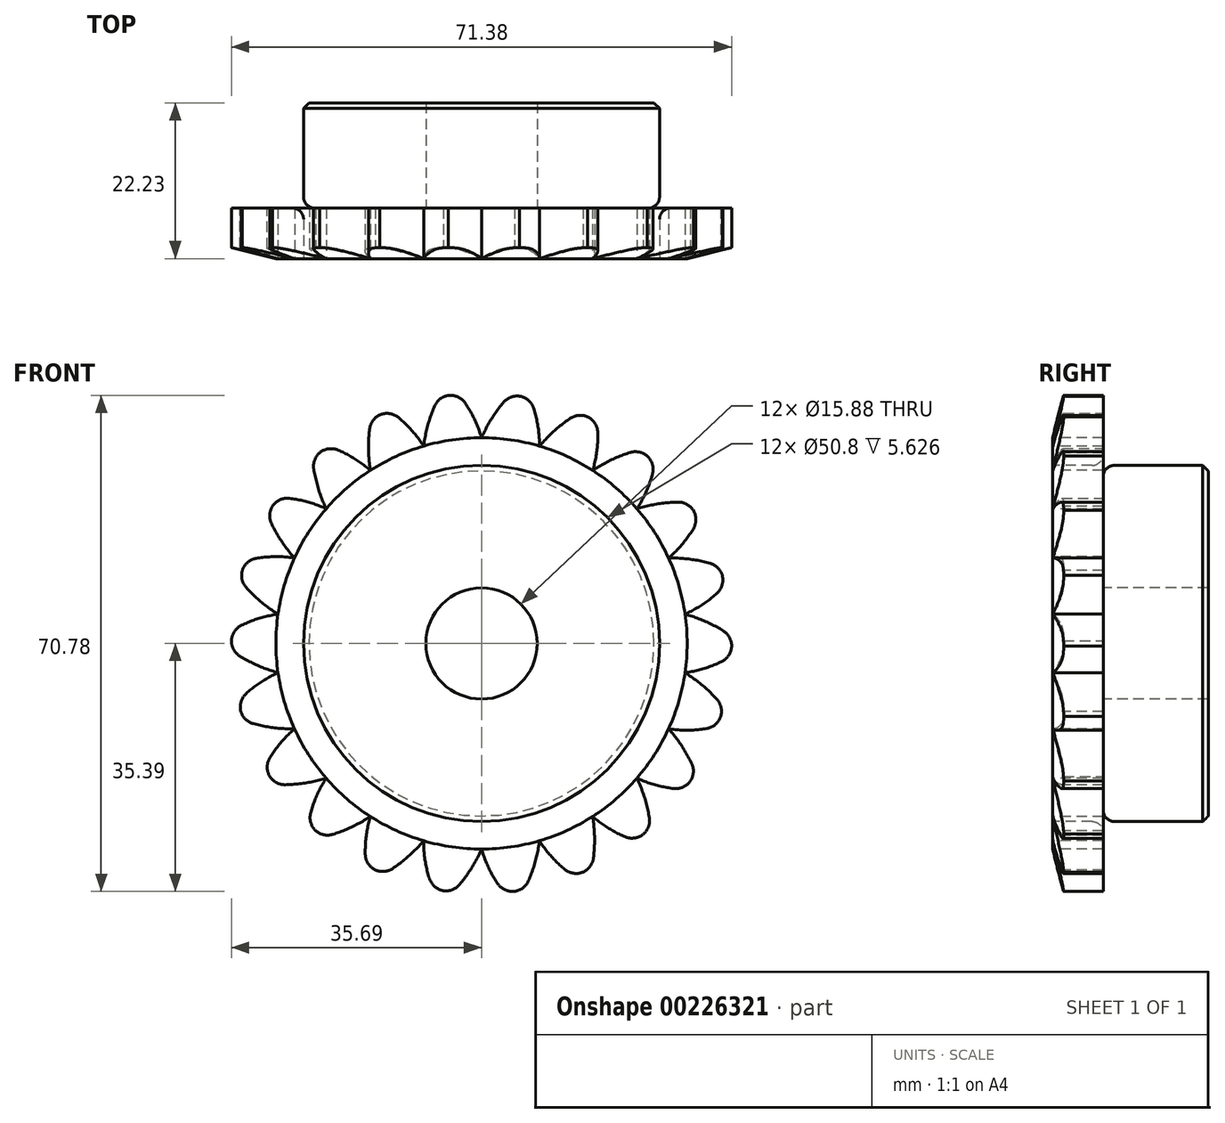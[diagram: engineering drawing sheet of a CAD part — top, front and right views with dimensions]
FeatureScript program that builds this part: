
annotation { "Feature Type Name" : "Feature", "Feature Type Description" : "" }
export const myFeature = defineFeature(function(context is Context, id is Id, definition is map)
    precondition{}
    {
        {
            var Q0;
            Q0=qCreatedBy(makeId("Right.planeOp"),FACE);
            var sketch = newSketch(context, id + "F0", { "sketchPlane" : qUnion([Q0])});
            skLineSegment(sketch, "E0", {"start": v(0, 0) * mm, "end": v(16.92, 0) * mm});
            skLineSegment(sketch, "E1.bottom", {"start": v(0, 7.94) * mm, "end": v(7.21, 7.94) * mm});
            skLineSegment(sketch, "E1.top", {"start": v(0, 35.69) * mm, "end": v(7.21, 35.69) * mm});
            skLineSegment(sketch, "E1.left", {"start": v(0, 7.94) * mm, "end": v(0, 35.69) * mm});
            skLineSegment(sketch, "E1.right", {"start": v(7.21, 7.94) * mm, "end": v(7.21, 35.69) * mm});
            skLineSegment(sketch, "E2.bottom", {"start": v(0, 7.94) * mm, "end": v(22.23, 7.94) * mm});
            skLineSegment(sketch, "E2.top", {"start": v(0, 25.4) * mm, "end": v(22.23, 25.4) * mm});
            skLineSegment(sketch, "E2.left", {"start": v(0, 7.94) * mm, "end": v(0, 25.4) * mm});
            skLineSegment(sketch, "E2.right", {"start": v(22.23, 7.94) * mm, "end": v(22.22, 25.4) * mm});
            skLineSegment(sketch, "E3.MirrorCS", {"start": v(0, -7.94) * mm, "end": v(7.21, -7.94) * mm});
            skLineSegment(sketch, "E4.MirrorCS", {"start": v(22.23, -7.94) * mm, "end": v(22.23, -25.4) * mm});
            skLineSegment(sketch, "E5.MirrorCS", {"start": v(0, -7.94) * mm, "end": v(0, -25.4) * mm});
            skLineSegment(sketch, "E6.MirrorCS", {"start": v(0, -35.69) * mm, "end": v(7.21, -35.69) * mm});
            skLineSegment(sketch, "E7.MirrorCS", {"start": v(0, -7.94) * mm, "end": v(0, -35.69) * mm});
            skLineSegment(sketch, "E8.MirrorCS", {"start": v(7.21, -7.94) * mm, "end": v(7.21, -35.69) * mm});
            skLineSegment(sketch, "E9.MirrorCS", {"start": v(0, -25.4) * mm, "end": v(22.23, -25.4) * mm});
            skLineSegment(sketch, "E10.MirrorCS", {"start": v(0, -7.94) * mm, "end": v(22.23, -7.94) * mm});
            skSolve(sketch);
        }
        {
            var Q0;
            {var subQ0=sQuery(id+"F0.wireOp",EDGE,"E1.top");Q0=makeQuery(id+"F0.imprint","IMPRINT",FACE,{"disambiguationData":[TD([[makeQuery(id+"F0.imprint","IMPRINT",EDGE,{"derivedFrom":subQ0}),-1.0]])]});}
            var Q1;
            {var subQ5=sQuery(id+"F0.wireOp",EDGE,"E2.left");Q1=makeQuery(id+"F0.imprint","IMPRINT",FACE,{"disambiguationData":[TD([[makeQuery(id+"F0.imprint","IMPRINT",EDGE,{"derivedFrom":subQ5}),-1.0]])]});}
            var Q2;
            {var subQ5=sQuery(id+"F0.wireOp",EDGE,"E2.right");Q2=makeQuery(id+"F0.imprint","IMPRINT",FACE,{"disambiguationData":[TD([[makeQuery(id+"F0.imprint","IMPRINT",EDGE,{"derivedFrom":subQ5}),1.0]])]});}
            var Q3;
            Q3=sQuery(id+"F0.wireOp",EDGE,"E0");
            revolve(context, id + "F1", {"entities" : qUnion([Q0, Q1, Q2]), "axis" : qUnion([Q3]), "revolveType" : RevolveType.FULL});
        }
        {
            var Q0;
            Q0=makeQuery(id+"F1.opRevolve","SWEPT_EDGE",EDGE,{"disambiguationData":[OSD([sQuery(id+"F0.wireOp",EDGE,"E1.right"),sQuery(id+"F0.wireOp",EDGE,"E2.top")])]});
            fillet(context, id + "F2", {"entities" : qUnion([Q0]), "radius" : 1.59 * mm, "tangentPropagation" : true, "allowEdgeOverflow" : false});
        }
        {
            var Q0;
            Q0=makeQuery(id+"F1.opRevolve","SWEPT_EDGE",EDGE,{"disambiguationData":[OSD([sQuery(id+"F0.wireOp",EDGE,"E2.top"),sQuery(id+"F0.wireOp",EDGE,"E2.right")])]});
            chamfer(context, id + "F3", {"entities" : qUnion([Q0]), "width" : 0.8 * mm, "tangentPropagation" : true});
        }
        {
            var Q0;
            Q0=makeQuery(id+"F1.opRevolve","SWEPT_EDGE",EDGE,{"disambiguationData":[OSD([sQuery(id+"F0.wireOp",EDGE,"E1.top"),sQuery(id+"F0.wireOp",EDGE,"E1.left")])]});
            chamfer(context, id + "F4", {"entities" : qUnion([Q0]), "chamferType" : ChamferType.TWO_OFFSETS, "width1" : 6.35 * mm, "oppositeDirection" : false, "width2" : 1.57 * mm, "tangentPropagation" : true});
        }
        {
            var Q0;
            Q0=qCreatedBy(makeId("Front.planeOp"),FACE);
            cPlane(context, id + "F5", {"entities" : qUnion([Q0]), "cplaneType" : CPlaneType.OFFSET, "offset" : 0 * mm, "oppositeDirection" : true, "width" : 152.4 * mm, "height" : 152.4 * mm});
        }
        {
            var Q0;
            Q0=qCreatedBy(id+"F5.planeOp",FACE);
            var sketch = newSketch(context, id + "F6", { "sketchPlane" : qUnion([Q0])});
            skArc(sketch, "E11", {"start": v(0, 29.34) * mm, "mid": v(-1.65, 33.21) * mm, "end": v(-4.18, 36.58) * mm});
            skArc(sketch, "E12", {"start": v(4.94, 36.31) * mm, "mid": v(2.12, 33.08) * mm, "end": v(0, 29.34) * mm});
            skArc(sketch, "E13", {"start": v(4.94, 36.31) * mm, "mid": v(0.4, 36.73) * mm, "end": v(-4.18, 36.58) * mm});
            skArc(sketch, "E14.1.0", {"start": v(-8.26, 28.15) * mm, "mid": v(-10.94, 31.4) * mm, "end": v(-14.32, 33.92) * mm});
            skArc(sketch, "E14.1.1", {"start": v(-5.49, 36.24) * mm, "mid": v(-7.29, 32.33) * mm, "end": v(-8.26, 28.15) * mm});
            skArc(sketch, "E14.1.2", {"start": v(-5.49, 36.24) * mm, "mid": v(-9.97, 35.35) * mm, "end": v(-14.32, 33.92) * mm});
            skArc(sketch, "E14.2.0", {"start": v(-15.86, 24.68) * mm, "mid": v(-19.34, 27.05) * mm, "end": v(-23.3, 28.52) * mm});
            skArc(sketch, "E14.2.1", {"start": v(-15.47, 33.22) * mm, "mid": v(-16.1, 28.97) * mm, "end": v(-15.86, 24.68) * mm});
            skArc(sketch, "E14.2.2", {"start": v(-15.47, 33.22) * mm, "mid": v(-19.53, 31.1) * mm, "end": v(-23.3, 28.52) * mm});
            skPoint(sketch, "E14.center", {"position": v(0, 0) * mm});
            skArc(sketch, "E15.1.3.0", {"start": v(-22.17, 19.21) * mm, "mid": v(-26.18, 20.5) * mm, "end": v(-30.38, 20.8) * mm});
            skArc(sketch, "E15.4.3.0", {"start": v(-24.2, 27.52) * mm, "mid": v(-23.61, 23.26) * mm, "end": v(-22.17, 19.21) * mm});
            skArc(sketch, "E15.8.3.0", {"start": v(-24.2, 27.52) * mm, "mid": v(-27.5, 24.34) * mm, "end": v(-30.38, 20.8) * mm});
            skArc(sketch, "E15.1.4.0", {"start": v(-26.68, 12.19) * mm, "mid": v(-30.9, 12.3) * mm, "end": v(-35.01, 11.4) * mm});
            skArc(sketch, "E15.4.4.0", {"start": v(-30.98, 19.58) * mm, "mid": v(-29.2, 15.66) * mm, "end": v(-26.68, 12.19) * mm});
            skArc(sketch, "E15.8.4.0", {"start": v(-30.98, 19.58) * mm, "mid": v(-33.24, 15.61) * mm, "end": v(-35.01, 11.4) * mm});
            skArc(sketch, "E15.1.5.0", {"start": v(-29.04, 4.17) * mm, "mid": v(-33.11, 3.1) * mm, "end": v(-36.8, 1.07) * mm});
            skArc(sketch, "E15.4.5.0", {"start": v(-35.24, 10.06) * mm, "mid": v(-32.44, 6.8) * mm, "end": v(-29.04, 4.17) * mm});
            skArc(sketch, "E15.8.5.0", {"start": v(-35.24, 10.06) * mm, "mid": v(-36.3, 5.61) * mm, "end": v(-36.8, 1.07) * mm});
            skArc(sketch, "E15.1.6.0", {"start": v(-29.04, -4.17) * mm, "mid": v(-32.64, -6.36) * mm, "end": v(-35.62, -9.34) * mm});
            skArc(sketch, "E15.4.6.0", {"start": v(-36.65, -0.28) * mm, "mid": v(-33.04, -2.61) * mm, "end": v(-29.04, -4.17) * mm});
            skArc(sketch, "E15.8.6.0", {"start": v(-36.65, -0.28) * mm, "mid": v(-36.4, -4.84) * mm, "end": v(-35.62, -9.34) * mm});
            skArc(sketch, "E16.1.7.0", {"start": v(-26.68, -12.19) * mm, "mid": v(-29.53, -15.3) * mm, "end": v(-31.54, -19) * mm});
            skArc(sketch, "E16.4.7.0", {"start": v(-35.09, -10.59) * mm, "mid": v(-30.97, -11.82) * mm, "end": v(-26.68, -12.19) * mm});
            skArc(sketch, "E16.8.7.0", {"start": v(-35.09, -10.59) * mm, "mid": v(-33.57, -14.9) * mm, "end": v(-31.54, -19) * mm});
            skArc(sketch, "E16.1.8.0", {"start": v(-22.17, -19.21) * mm, "mid": v(-24.02, -23) * mm, "end": v(-24.91, -27.11) * mm});
            skArc(sketch, "E16.4.8.0", {"start": v(-30.68, -20.05) * mm, "mid": v(-26.38, -20.06) * mm, "end": v(-22.17, -19.21) * mm});
            skArc(sketch, "E16.8.8.0", {"start": v(-30.68, -20.05) * mm, "mid": v(-28.01, -23.76) * mm, "end": v(-24.91, -27.11) * mm});
            skArc(sketch, "E16.1.9.0", {"start": v(-15.86, -24.68) * mm, "mid": v(-16.57, -28.83) * mm, "end": v(-16.26, -33.03) * mm});
            skArc(sketch, "E16.4.9.0", {"start": v(-23.8, -27.88) * mm, "mid": v(-19.66, -26.68) * mm, "end": v(-15.86, -24.68) * mm});
            skArc(sketch, "E16.8.9.0", {"start": v(-23.8, -27.88) * mm, "mid": v(-20.18, -30.68) * mm, "end": v(-16.26, -33.03) * mm});
            skArc(sketch, "E17.1.10.0", {"start": v(-8.26, -28.15) * mm, "mid": v(-7.78, -32.33) * mm, "end": v(-6.3, -36.28) * mm});
            skArc(sketch, "E17.4.10.0", {"start": v(-14.97, -33.45) * mm, "mid": v(-11.35, -31.14) * mm, "end": v(-8.26, -28.15) * mm});
            skArc(sketch, "E17.8.10.0", {"start": v(-14.97, -33.45) * mm, "mid": v(-10.72, -35.13) * mm, "end": v(-6.3, -36.28) * mm});
            skArc(sketch, "E17.1.11.0", {"start": v(0, -29.34) * mm, "mid": v(1.65, -33.21) * mm, "end": v(4.18, -36.58) * mm});
            skArc(sketch, "E17.4.11.0", {"start": v(-4.94, -36.31) * mm, "mid": v(-2.12, -33.08) * mm, "end": v(0, -29.34) * mm});
            skArc(sketch, "E17.8.11.0", {"start": v(-4.94, -36.31) * mm, "mid": v(-0.4, -36.73) * mm, "end": v(4.18, -36.58) * mm});
            skArc(sketch, "E17.1.12.0", {"start": v(8.26, -28.15) * mm, "mid": v(10.94, -31.4) * mm, "end": v(14.32, -33.92) * mm});
            skArc(sketch, "E17.4.12.0", {"start": v(5.49, -36.24) * mm, "mid": v(7.29, -32.33) * mm, "end": v(8.26, -28.15) * mm});
            skArc(sketch, "E17.8.12.0", {"start": v(5.49, -36.24) * mm, "mid": v(9.97, -35.35) * mm, "end": v(14.32, -33.92) * mm});
            skArc(sketch, "E17.1.13.0", {"start": v(15.86, -24.68) * mm, "mid": v(19.34, -27.05) * mm, "end": v(23.3, -28.52) * mm});
            skArc(sketch, "E17.4.13.0", {"start": v(15.47, -33.22) * mm, "mid": v(16.1, -28.97) * mm, "end": v(15.86, -24.68) * mm});
            skArc(sketch, "E17.8.13.0", {"start": v(15.47, -33.22) * mm, "mid": v(19.53, -31.1) * mm, "end": v(23.3, -28.52) * mm});
            skArc(sketch, "E17.1.14.0", {"start": v(22.17, -19.21) * mm, "mid": v(26.18, -20.5) * mm, "end": v(30.38, -20.8) * mm});
            skArc(sketch, "E17.4.14.0", {"start": v(24.2, -27.52) * mm, "mid": v(23.61, -23.26) * mm, "end": v(22.17, -19.21) * mm});
            skArc(sketch, "E17.8.14.0", {"start": v(24.2, -27.52) * mm, "mid": v(27.5, -24.34) * mm, "end": v(30.38, -20.8) * mm});
            skArc(sketch, "E18.1.15.0", {"start": v(26.68, -12.19) * mm, "mid": v(30.9, -12.3) * mm, "end": v(35.01, -11.4) * mm});
            skArc(sketch, "E18.4.15.0", {"start": v(30.98, -19.58) * mm, "mid": v(29.2, -15.66) * mm, "end": v(26.68, -12.19) * mm});
            skArc(sketch, "E18.8.15.0", {"start": v(30.98, -19.58) * mm, "mid": v(33.24, -15.61) * mm, "end": v(35.01, -11.4) * mm});
            skArc(sketch, "E18.1.16.0", {"start": v(29.04, -4.17) * mm, "mid": v(33.11, -3.1) * mm, "end": v(36.8, -1.07) * mm});
            skArc(sketch, "E18.4.16.0", {"start": v(35.24, -10.06) * mm, "mid": v(32.44, -6.8) * mm, "end": v(29.04, -4.17) * mm});
            skArc(sketch, "E18.8.16.0", {"start": v(35.24, -10.06) * mm, "mid": v(36.3, -5.61) * mm, "end": v(36.8, -1.07) * mm});
            skArc(sketch, "E19.1.17.0", {"start": v(29.04, 4.17) * mm, "mid": v(32.64, 6.36) * mm, "end": v(35.62, 9.34) * mm});
            skArc(sketch, "E19.4.17.0", {"start": v(36.65, 0.28) * mm, "mid": v(33.04, 2.61) * mm, "end": v(29.04, 4.17) * mm});
            skArc(sketch, "E19.8.17.0", {"start": v(36.65, 0.28) * mm, "mid": v(36.4, 4.84) * mm, "end": v(35.62, 9.34) * mm});
            skArc(sketch, "E19.1.18.0", {"start": v(26.68, 12.19) * mm, "mid": v(29.53, 15.3) * mm, "end": v(31.54, 19) * mm});
            skArc(sketch, "E19.4.18.0", {"start": v(35.09, 10.59) * mm, "mid": v(30.97, 11.82) * mm, "end": v(26.68, 12.19) * mm});
            skArc(sketch, "E19.8.18.0", {"start": v(35.09, 10.59) * mm, "mid": v(33.57, 14.9) * mm, "end": v(31.54, 19) * mm});
            skArc(sketch, "E19.1.19.0", {"start": v(22.17, 19.21) * mm, "mid": v(24.02, 23) * mm, "end": v(24.91, 27.11) * mm});
            skArc(sketch, "E19.4.19.0", {"start": v(30.68, 20.05) * mm, "mid": v(26.38, 20.06) * mm, "end": v(22.17, 19.21) * mm});
            skArc(sketch, "E19.8.19.0", {"start": v(30.68, 20.05) * mm, "mid": v(28.01, 23.76) * mm, "end": v(24.91, 27.11) * mm});
            skArc(sketch, "E20.1.20.0", {"start": v(15.86, 24.68) * mm, "mid": v(16.57, 28.83) * mm, "end": v(16.26, 33.03) * mm});
            skArc(sketch, "E20.4.20.0", {"start": v(23.8, 27.88) * mm, "mid": v(19.66, 26.68) * mm, "end": v(15.86, 24.68) * mm});
            skArc(sketch, "E20.8.20.0", {"start": v(23.8, 27.88) * mm, "mid": v(20.18, 30.68) * mm, "end": v(16.26, 33.03) * mm});
            skArc(sketch, "E20.1.21.0", {"start": v(8.26, 28.15) * mm, "mid": v(7.78, 32.33) * mm, "end": v(6.3, 36.28) * mm});
            skArc(sketch, "E20.4.21.0", {"start": v(14.97, 33.45) * mm, "mid": v(11.35, 31.14) * mm, "end": v(8.26, 28.15) * mm});
            skArc(sketch, "E20.8.21.0", {"start": v(14.97, 33.45) * mm, "mid": v(10.72, 35.13) * mm, "end": v(6.3, 36.28) * mm});
            skSolve(sketch);
        }
        {
            var Q0;
            Q0=makeQuery(id+"F6.imprint","IMPRINT",FACE,{"disambiguationData":[TD([[makeQuery(id+"F6.imprint","IMPRINT",EDGE,{"derivedFrom":sQuery(id+"F6.wireOp",EDGE,"E11")}),-1.0]])]});
            var Q1;
            Q1=makeQuery(id+"F6.imprint","IMPRINT",FACE,{"disambiguationData":[TD([[makeQuery(id+"F6.imprint","IMPRINT",EDGE,{"derivedFrom":sQuery(id+"F6.wireOp",EDGE,"E14.2.0")}),-1.0]])]});
            var Q2;
            Q2=makeQuery(id+"F6.imprint","IMPRINT",FACE,{"disambiguationData":[TD([[makeQuery(id+"F6.imprint","IMPRINT",EDGE,{"derivedFrom":sQuery(id+"F6.wireOp",EDGE,"E14.1.0")}),-1.0]])]});
            var Q3;
            Q3=makeQuery(id+"F6.imprint","IMPRINT",FACE,{"disambiguationData":[TD([[makeQuery(id+"F6.imprint","IMPRINT",EDGE,{"derivedFrom":sQuery(id+"F6.wireOp",EDGE,"E20.1.21.0")}),-1.0]])]});
            var Q4;
            Q4=makeQuery(id+"F6.imprint","IMPRINT",FACE,{"disambiguationData":[TD([[makeQuery(id+"F6.imprint","IMPRINT",EDGE,{"derivedFrom":sQuery(id+"F6.wireOp",EDGE,"E20.1.20.0")}),-1.0]])]});
            var Q5;
            Q5=makeQuery(id+"F6.imprint","IMPRINT",FACE,{"disambiguationData":[TD([[makeQuery(id+"F6.imprint","IMPRINT",EDGE,{"derivedFrom":sQuery(id+"F6.wireOp",EDGE,"E19.1.19.0")}),-1.0]])]});
            var Q6;
            Q6=makeQuery(id+"F6.imprint","IMPRINT",FACE,{"disambiguationData":[TD([[makeQuery(id+"F6.imprint","IMPRINT",EDGE,{"derivedFrom":sQuery(id+"F6.wireOp",EDGE,"E19.1.18.0")}),-1.0]])]});
            var Q7;
            Q7=makeQuery(id+"F6.imprint","IMPRINT",FACE,{"disambiguationData":[TD([[makeQuery(id+"F6.imprint","IMPRINT",EDGE,{"derivedFrom":sQuery(id+"F6.wireOp",EDGE,"E19.1.17.0")}),-1.0]])]});
            var Q8;
            Q8=makeQuery(id+"F6.imprint","IMPRINT",FACE,{"disambiguationData":[TD([[makeQuery(id+"F6.imprint","IMPRINT",EDGE,{"derivedFrom":sQuery(id+"F6.wireOp",EDGE,"E18.1.16.0")}),-1.0]])]});
            var Q9;
            Q9=makeQuery(id+"F6.imprint","IMPRINT",FACE,{"disambiguationData":[TD([[makeQuery(id+"F6.imprint","IMPRINT",EDGE,{"derivedFrom":sQuery(id+"F6.wireOp",EDGE,"E18.1.15.0")}),-1.0]])]});
            var Q10;
            Q10=makeQuery(id+"F6.imprint","IMPRINT",FACE,{"disambiguationData":[TD([[makeQuery(id+"F6.imprint","IMPRINT",EDGE,{"derivedFrom":sQuery(id+"F6.wireOp",EDGE,"E17.1.14.0")}),-1.0]])]});
            var Q11;
            Q11=makeQuery(id+"F6.imprint","IMPRINT",FACE,{"disambiguationData":[TD([[makeQuery(id+"F6.imprint","IMPRINT",EDGE,{"derivedFrom":sQuery(id+"F6.wireOp",EDGE,"E17.1.13.0")}),-1.0]])]});
            var Q12;
            Q12=makeQuery(id+"F6.imprint","IMPRINT",FACE,{"disambiguationData":[TD([[makeQuery(id+"F6.imprint","IMPRINT",EDGE,{"derivedFrom":sQuery(id+"F6.wireOp",EDGE,"E17.1.12.0")}),-1.0]])]});
            var Q13;
            Q13=makeQuery(id+"F6.imprint","IMPRINT",FACE,{"disambiguationData":[TD([[makeQuery(id+"F6.imprint","IMPRINT",EDGE,{"derivedFrom":sQuery(id+"F6.wireOp",EDGE,"E17.1.11.0")}),-1.0]])]});
            var Q14;
            Q14=makeQuery(id+"F6.imprint","IMPRINT",FACE,{"disambiguationData":[TD([[makeQuery(id+"F6.imprint","IMPRINT",EDGE,{"derivedFrom":sQuery(id+"F6.wireOp",EDGE,"E17.1.10.0")}),-1.0]])]});
            var Q15;
            Q15=makeQuery(id+"F6.imprint","IMPRINT",FACE,{"disambiguationData":[TD([[makeQuery(id+"F6.imprint","IMPRINT",EDGE,{"derivedFrom":sQuery(id+"F6.wireOp",EDGE,"E16.1.9.0")}),-1.0]])]});
            var Q16;
            Q16=makeQuery(id+"F6.imprint","IMPRINT",FACE,{"disambiguationData":[TD([[makeQuery(id+"F6.imprint","IMPRINT",EDGE,{"derivedFrom":sQuery(id+"F6.wireOp",EDGE,"E16.1.8.0")}),-1.0]])]});
            var Q17;
            Q17=makeQuery(id+"F6.imprint","IMPRINT",FACE,{"disambiguationData":[TD([[makeQuery(id+"F6.imprint","IMPRINT",EDGE,{"derivedFrom":sQuery(id+"F6.wireOp",EDGE,"E16.1.7.0")}),-1.0]])]});
            var Q18;
            Q18=makeQuery(id+"F6.imprint","IMPRINT",FACE,{"disambiguationData":[TD([[makeQuery(id+"F6.imprint","IMPRINT",EDGE,{"derivedFrom":sQuery(id+"F6.wireOp",EDGE,"E15.1.6.0")}),-1.0]])]});
            var Q19;
            Q19=makeQuery(id+"F6.imprint","IMPRINT",FACE,{"disambiguationData":[TD([[makeQuery(id+"F6.imprint","IMPRINT",EDGE,{"derivedFrom":sQuery(id+"F6.wireOp",EDGE,"E15.1.5.0")}),-1.0]])]});
            var Q20;
            Q20=makeQuery(id+"F6.imprint","IMPRINT",FACE,{"disambiguationData":[TD([[makeQuery(id+"F6.imprint","IMPRINT",EDGE,{"derivedFrom":sQuery(id+"F6.wireOp",EDGE,"E15.1.4.0")}),-1.0]])]});
            var Q21;
            Q21=makeQuery(id+"F6.imprint","IMPRINT",FACE,{"disambiguationData":[TD([[makeQuery(id+"F6.imprint","IMPRINT",EDGE,{"derivedFrom":sQuery(id+"F6.wireOp",EDGE,"E15.1.3.0")}),-1.0]])]});
            extrude(context, id + "F7", {"entities" : qUnion([Q0, Q1, Q2, Q3, Q4, Q5, Q6, Q7, Q8, Q9, Q10, Q11, Q12, Q13, Q14, Q15, Q16, Q17, Q18, Q19, Q20, Q21]), "operationType" : NewBodyOperationType.REMOVE, "oppositeDirection" : true, "depth" : 7.87 * mm});
        }
        {
            var Q0;
            Q0=makeQuery(id+"F7.boolean.opBoolean","INTERSECT",EDGE,{"derivedFrom":[makeQuery(id+"F1.opRevolve","SWEPT_FACE",FACE,{"disambiguationData":[OSD([sQuery(id+"F0.wireOp",EDGE,"E1.top")])]}),makeQuery(id+"F7.opExtrude","SWEPT_FACE",FACE,{"disambiguationData":[OSD([sQuery(id+"F6.wireOp",EDGE,"E17.4.13.0")])]})]});
            var Q1;
            Q1=makeQuery(id+"F7.boolean.opBoolean","INTERSECT",EDGE,{"derivedFrom":[makeQuery(id+"F1.opRevolve","SWEPT_FACE",FACE,{"disambiguationData":[OSD([sQuery(id+"F0.wireOp",EDGE,"E1.top")])]}),makeQuery(id+"F7.opExtrude","SWEPT_FACE",FACE,{"disambiguationData":[OSD([sQuery(id+"F6.wireOp",EDGE,"E17.1.12.0")])]})]});
            var Q2;
            Q2=makeQuery(id+"F7.boolean.opBoolean","INTERSECT",EDGE,{"derivedFrom":[makeQuery(id+"F1.opRevolve","SWEPT_FACE",FACE,{"disambiguationData":[OSD([sQuery(id+"F0.wireOp",EDGE,"E1.top")])]}),makeQuery(id+"F7.opExtrude","SWEPT_FACE",FACE,{"disambiguationData":[OSD([sQuery(id+"F6.wireOp",EDGE,"E17.4.12.0")])]})]});
            var Q3;
            Q3=makeQuery(id+"F7.boolean.opBoolean","INTERSECT",EDGE,{"derivedFrom":[makeQuery(id+"F1.opRevolve","SWEPT_FACE",FACE,{"disambiguationData":[OSD([sQuery(id+"F0.wireOp",EDGE,"E1.top")])]}),makeQuery(id+"F7.opExtrude","SWEPT_FACE",FACE,{"disambiguationData":[OSD([sQuery(id+"F6.wireOp",EDGE,"E17.1.11.0")])]})]});
            var Q4;
            Q4=makeQuery(id+"F7.boolean.opBoolean","INTERSECT",EDGE,{"derivedFrom":[makeQuery(id+"F1.opRevolve","SWEPT_FACE",FACE,{"disambiguationData":[OSD([sQuery(id+"F0.wireOp",EDGE,"E1.top")])]}),makeQuery(id+"F7.opExtrude","SWEPT_FACE",FACE,{"disambiguationData":[OSD([sQuery(id+"F6.wireOp",EDGE,"E17.4.11.0")])]})]});
            var Q5;
            Q5=makeQuery(id+"F7.boolean.opBoolean","INTERSECT",EDGE,{"derivedFrom":[makeQuery(id+"F1.opRevolve","SWEPT_FACE",FACE,{"disambiguationData":[OSD([sQuery(id+"F0.wireOp",EDGE,"E1.top")])]}),makeQuery(id+"F7.opExtrude","SWEPT_FACE",FACE,{"disambiguationData":[OSD([sQuery(id+"F6.wireOp",EDGE,"E17.1.10.0")])]})]});
            var Q6;
            Q6=makeQuery(id+"F7.boolean.opBoolean","INTERSECT",EDGE,{"derivedFrom":[makeQuery(id+"F1.opRevolve","SWEPT_FACE",FACE,{"disambiguationData":[OSD([sQuery(id+"F0.wireOp",EDGE,"E1.top")])]}),makeQuery(id+"F7.opExtrude","SWEPT_FACE",FACE,{"disambiguationData":[OSD([sQuery(id+"F6.wireOp",EDGE,"E17.4.10.0")])]})]});
            var Q7;
            Q7=makeQuery(id+"F7.boolean.opBoolean","INTERSECT",EDGE,{"derivedFrom":[makeQuery(id+"F1.opRevolve","SWEPT_FACE",FACE,{"disambiguationData":[OSD([sQuery(id+"F0.wireOp",EDGE,"E1.top")])]}),makeQuery(id+"F7.opExtrude","SWEPT_FACE",FACE,{"disambiguationData":[OSD([sQuery(id+"F6.wireOp",EDGE,"E16.1.9.0")])]})]});
            var Q8;
            Q8=makeQuery(id+"F7.boolean.opBoolean","INTERSECT",EDGE,{"derivedFrom":[makeQuery(id+"F1.opRevolve","SWEPT_FACE",FACE,{"disambiguationData":[OSD([sQuery(id+"F0.wireOp",EDGE,"E1.top")])]}),makeQuery(id+"F7.opExtrude","SWEPT_FACE",FACE,{"disambiguationData":[OSD([sQuery(id+"F6.wireOp",EDGE,"E16.4.9.0")])]})]});
            var Q9;
            Q9=makeQuery(id+"F7.boolean.opBoolean","INTERSECT",EDGE,{"derivedFrom":[makeQuery(id+"F1.opRevolve","SWEPT_FACE",FACE,{"disambiguationData":[OSD([sQuery(id+"F0.wireOp",EDGE,"E1.top")])]}),makeQuery(id+"F7.opExtrude","SWEPT_FACE",FACE,{"disambiguationData":[OSD([sQuery(id+"F6.wireOp",EDGE,"E16.1.8.0")])]})]});
            var Q10;
            Q10=makeQuery(id+"F7.boolean.opBoolean","INTERSECT",EDGE,{"derivedFrom":[makeQuery(id+"F1.opRevolve","SWEPT_FACE",FACE,{"disambiguationData":[OSD([sQuery(id+"F0.wireOp",EDGE,"E1.top")])]}),makeQuery(id+"F7.opExtrude","SWEPT_FACE",FACE,{"disambiguationData":[OSD([sQuery(id+"F6.wireOp",EDGE,"E16.1.7.0")])]})]});
            var Q11;
            Q11=makeQuery(id+"F7.boolean.opBoolean","INTERSECT",EDGE,{"derivedFrom":[makeQuery(id+"F1.opRevolve","SWEPT_FACE",FACE,{"disambiguationData":[OSD([sQuery(id+"F0.wireOp",EDGE,"E1.top")])]}),makeQuery(id+"F7.opExtrude","SWEPT_FACE",FACE,{"disambiguationData":[OSD([sQuery(id+"F6.wireOp",EDGE,"E16.4.8.0")])]})]});
            var Q12;
            Q12=makeQuery(id+"F7.boolean.opBoolean","INTERSECT",EDGE,{"derivedFrom":[makeQuery(id+"F1.opRevolve","SWEPT_FACE",FACE,{"disambiguationData":[OSD([sQuery(id+"F0.wireOp",EDGE,"E1.top")])]}),makeQuery(id+"F7.opExtrude","SWEPT_FACE",FACE,{"disambiguationData":[OSD([sQuery(id+"F6.wireOp",EDGE,"E16.4.7.0")])]})]});
            var Q13;
            Q13=makeQuery(id+"F7.boolean.opBoolean","INTERSECT",EDGE,{"derivedFrom":[makeQuery(id+"F1.opRevolve","SWEPT_FACE",FACE,{"disambiguationData":[OSD([sQuery(id+"F0.wireOp",EDGE,"E1.top")])]}),makeQuery(id+"F7.opExtrude","SWEPT_FACE",FACE,{"disambiguationData":[OSD([sQuery(id+"F6.wireOp",EDGE,"E15.1.5.0")])]})]});
            var Q14;
            Q14=makeQuery(id+"F7.boolean.opBoolean","INTERSECT",EDGE,{"derivedFrom":[makeQuery(id+"F1.opRevolve","SWEPT_FACE",FACE,{"disambiguationData":[OSD([sQuery(id+"F0.wireOp",EDGE,"E1.top")])]}),makeQuery(id+"F7.opExtrude","SWEPT_FACE",FACE,{"disambiguationData":[OSD([sQuery(id+"F6.wireOp",EDGE,"E15.4.6.0")])]})]});
            var Q15;
            Q15=makeQuery(id+"F7.boolean.opBoolean","INTERSECT",EDGE,{"derivedFrom":[makeQuery(id+"F1.opRevolve","SWEPT_FACE",FACE,{"disambiguationData":[OSD([sQuery(id+"F0.wireOp",EDGE,"E1.top")])]}),makeQuery(id+"F7.opExtrude","SWEPT_FACE",FACE,{"disambiguationData":[OSD([sQuery(id+"F6.wireOp",EDGE,"E15.4.5.0")])]})]});
            var Q16;
            Q16=makeQuery(id+"F7.boolean.opBoolean","INTERSECT",EDGE,{"derivedFrom":[makeQuery(id+"F1.opRevolve","SWEPT_FACE",FACE,{"disambiguationData":[OSD([sQuery(id+"F0.wireOp",EDGE,"E1.top")])]}),makeQuery(id+"F7.opExtrude","SWEPT_FACE",FACE,{"disambiguationData":[OSD([sQuery(id+"F6.wireOp",EDGE,"E15.1.4.0")])]})]});
            var Q17;
            Q17=makeQuery(id+"F7.boolean.opBoolean","INTERSECT",EDGE,{"derivedFrom":[makeQuery(id+"F1.opRevolve","SWEPT_FACE",FACE,{"disambiguationData":[OSD([sQuery(id+"F0.wireOp",EDGE,"E1.top")])]}),makeQuery(id+"F7.opExtrude","SWEPT_FACE",FACE,{"disambiguationData":[OSD([sQuery(id+"F6.wireOp",EDGE,"E15.4.4.0")])]})]});
            var Q18;
            Q18=makeQuery(id+"F7.boolean.opBoolean","INTERSECT",EDGE,{"derivedFrom":[makeQuery(id+"F1.opRevolve","SWEPT_FACE",FACE,{"disambiguationData":[OSD([sQuery(id+"F0.wireOp",EDGE,"E1.top")])]}),makeQuery(id+"F7.opExtrude","SWEPT_FACE",FACE,{"disambiguationData":[OSD([sQuery(id+"F6.wireOp",EDGE,"E15.1.3.0")])]})]});
            var Q19;
            Q19=makeQuery(id+"F7.boolean.opBoolean","INTERSECT",EDGE,{"derivedFrom":[makeQuery(id+"F1.opRevolve","SWEPT_FACE",FACE,{"disambiguationData":[OSD([sQuery(id+"F0.wireOp",EDGE,"E1.top")])]}),makeQuery(id+"F7.opExtrude","SWEPT_FACE",FACE,{"disambiguationData":[OSD([sQuery(id+"F6.wireOp",EDGE,"E15.4.3.0")])]})]});
            var Q20;
            Q20=makeQuery(id+"F7.boolean.opBoolean","INTERSECT",EDGE,{"derivedFrom":[makeQuery(id+"F1.opRevolve","SWEPT_FACE",FACE,{"disambiguationData":[OSD([sQuery(id+"F0.wireOp",EDGE,"E1.top")])]}),makeQuery(id+"F7.opExtrude","SWEPT_FACE",FACE,{"disambiguationData":[OSD([sQuery(id+"F6.wireOp",EDGE,"E14.2.0")])]})]});
            var Q21;
            Q21=makeQuery(id+"F7.boolean.opBoolean","INTERSECT",EDGE,{"derivedFrom":[makeQuery(id+"F1.opRevolve","SWEPT_FACE",FACE,{"disambiguationData":[OSD([sQuery(id+"F0.wireOp",EDGE,"E1.top")])]}),makeQuery(id+"F7.opExtrude","SWEPT_FACE",FACE,{"disambiguationData":[OSD([sQuery(id+"F6.wireOp",EDGE,"E14.2.1")])]})]});
            var Q22;
            Q22=makeQuery(id+"F7.boolean.opBoolean","INTERSECT",EDGE,{"derivedFrom":[makeQuery(id+"F1.opRevolve","SWEPT_FACE",FACE,{"disambiguationData":[OSD([sQuery(id+"F0.wireOp",EDGE,"E1.top")])]}),makeQuery(id+"F7.opExtrude","SWEPT_FACE",FACE,{"disambiguationData":[OSD([sQuery(id+"F6.wireOp",EDGE,"E14.1.0")])]})]});
            var Q23;
            Q23=makeQuery(id+"F7.boolean.opBoolean","INTERSECT",EDGE,{"derivedFrom":[makeQuery(id+"F1.opRevolve","SWEPT_FACE",FACE,{"disambiguationData":[OSD([sQuery(id+"F0.wireOp",EDGE,"E1.top")])]}),makeQuery(id+"F7.opExtrude","SWEPT_FACE",FACE,{"disambiguationData":[OSD([sQuery(id+"F6.wireOp",EDGE,"E14.1.1")])]})]});
            var Q24;
            Q24=makeQuery(id+"F7.boolean.opBoolean","INTERSECT",EDGE,{"derivedFrom":[makeQuery(id+"F1.opRevolve","SWEPT_FACE",FACE,{"disambiguationData":[OSD([sQuery(id+"F0.wireOp",EDGE,"E1.top")])]}),makeQuery(id+"F7.opExtrude","SWEPT_FACE",FACE,{"disambiguationData":[OSD([sQuery(id+"F6.wireOp",EDGE,"E11")])]})]});
            var Q25;
            Q25=makeQuery(id+"F7.boolean.opBoolean","INTERSECT",EDGE,{"derivedFrom":[makeQuery(id+"F1.opRevolve","SWEPT_FACE",FACE,{"disambiguationData":[OSD([sQuery(id+"F0.wireOp",EDGE,"E1.top")])]}),makeQuery(id+"F7.opExtrude","SWEPT_FACE",FACE,{"disambiguationData":[OSD([sQuery(id+"F6.wireOp",EDGE,"E12")])]})]});
            var Q26;
            Q26=makeQuery(id+"F7.boolean.opBoolean","INTERSECT",EDGE,{"derivedFrom":[makeQuery(id+"F1.opRevolve","SWEPT_FACE",FACE,{"disambiguationData":[OSD([sQuery(id+"F0.wireOp",EDGE,"E1.top")])]}),makeQuery(id+"F7.opExtrude","SWEPT_FACE",FACE,{"disambiguationData":[OSD([sQuery(id+"F6.wireOp",EDGE,"E20.1.21.0")])]})]});
            var Q27;
            Q27=makeQuery(id+"F7.boolean.opBoolean","INTERSECT",EDGE,{"derivedFrom":[makeQuery(id+"F1.opRevolve","SWEPT_FACE",FACE,{"disambiguationData":[OSD([sQuery(id+"F0.wireOp",EDGE,"E1.top")])]}),makeQuery(id+"F7.opExtrude","SWEPT_FACE",FACE,{"disambiguationData":[OSD([sQuery(id+"F6.wireOp",EDGE,"E20.4.21.0")])]})]});
            var Q28;
            Q28=makeQuery(id+"F7.boolean.opBoolean","INTERSECT",EDGE,{"derivedFrom":[makeQuery(id+"F1.opRevolve","SWEPT_FACE",FACE,{"disambiguationData":[OSD([sQuery(id+"F0.wireOp",EDGE,"E1.top")])]}),makeQuery(id+"F7.opExtrude","SWEPT_FACE",FACE,{"disambiguationData":[OSD([sQuery(id+"F6.wireOp",EDGE,"E20.1.20.0")])]})]});
            var Q29;
            Q29=makeQuery(id+"F7.boolean.opBoolean","INTERSECT",EDGE,{"derivedFrom":[makeQuery(id+"F1.opRevolve","SWEPT_FACE",FACE,{"disambiguationData":[OSD([sQuery(id+"F0.wireOp",EDGE,"E1.top")])]}),makeQuery(id+"F7.opExtrude","SWEPT_FACE",FACE,{"disambiguationData":[OSD([sQuery(id+"F6.wireOp",EDGE,"E19.1.19.0")])]})]});
            var Q30;
            Q30=makeQuery(id+"F7.boolean.opBoolean","INTERSECT",EDGE,{"derivedFrom":[makeQuery(id+"F1.opRevolve","SWEPT_FACE",FACE,{"disambiguationData":[OSD([sQuery(id+"F0.wireOp",EDGE,"E1.top")])]}),makeQuery(id+"F7.opExtrude","SWEPT_FACE",FACE,{"disambiguationData":[OSD([sQuery(id+"F6.wireOp",EDGE,"E20.4.20.0")])]})]});
            var Q31;
            Q31=makeQuery(id+"F7.boolean.opBoolean","INTERSECT",EDGE,{"derivedFrom":[makeQuery(id+"F1.opRevolve","SWEPT_FACE",FACE,{"disambiguationData":[OSD([sQuery(id+"F0.wireOp",EDGE,"E1.top")])]}),makeQuery(id+"F7.opExtrude","SWEPT_FACE",FACE,{"disambiguationData":[OSD([sQuery(id+"F6.wireOp",EDGE,"E19.4.19.0")])]})]});
            var Q32;
            Q32=makeQuery(id+"F7.boolean.opBoolean","INTERSECT",EDGE,{"derivedFrom":[makeQuery(id+"F1.opRevolve","SWEPT_FACE",FACE,{"disambiguationData":[OSD([sQuery(id+"F0.wireOp",EDGE,"E1.top")])]}),makeQuery(id+"F7.opExtrude","SWEPT_FACE",FACE,{"disambiguationData":[OSD([sQuery(id+"F6.wireOp",EDGE,"E19.1.18.0")])]})]});
            var Q33;
            Q33=makeQuery(id+"F7.boolean.opBoolean","INTERSECT",EDGE,{"derivedFrom":[makeQuery(id+"F1.opRevolve","SWEPT_FACE",FACE,{"disambiguationData":[OSD([sQuery(id+"F0.wireOp",EDGE,"E1.top")])]}),makeQuery(id+"F7.opExtrude","SWEPT_FACE",FACE,{"disambiguationData":[OSD([sQuery(id+"F6.wireOp",EDGE,"E19.1.17.0")])]})]});
            var Q34;
            Q34=makeQuery(id+"F7.boolean.opBoolean","INTERSECT",EDGE,{"derivedFrom":[makeQuery(id+"F1.opRevolve","SWEPT_FACE",FACE,{"disambiguationData":[OSD([sQuery(id+"F0.wireOp",EDGE,"E1.top")])]}),makeQuery(id+"F7.opExtrude","SWEPT_FACE",FACE,{"disambiguationData":[OSD([sQuery(id+"F6.wireOp",EDGE,"E19.4.18.0")])]})]});
            var Q35;
            Q35=makeQuery(id+"F7.boolean.opBoolean","INTERSECT",EDGE,{"derivedFrom":[makeQuery(id+"F1.opRevolve","SWEPT_FACE",FACE,{"disambiguationData":[OSD([sQuery(id+"F0.wireOp",EDGE,"E1.top")])]}),makeQuery(id+"F7.opExtrude","SWEPT_FACE",FACE,{"disambiguationData":[OSD([sQuery(id+"F6.wireOp",EDGE,"E19.4.17.0")])]})]});
            var Q36;
            Q36=makeQuery(id+"F7.boolean.opBoolean","INTERSECT",EDGE,{"derivedFrom":[makeQuery(id+"F1.opRevolve","SWEPT_FACE",FACE,{"disambiguationData":[OSD([sQuery(id+"F0.wireOp",EDGE,"E1.top")])]}),makeQuery(id+"F7.opExtrude","SWEPT_FACE",FACE,{"disambiguationData":[OSD([sQuery(id+"F6.wireOp",EDGE,"E18.1.16.0")])]})]});
            var Q37;
            Q37=makeQuery(id+"F7.boolean.opBoolean","INTERSECT",EDGE,{"derivedFrom":[makeQuery(id+"F1.opRevolve","SWEPT_FACE",FACE,{"disambiguationData":[OSD([sQuery(id+"F0.wireOp",EDGE,"E1.top")])]}),makeQuery(id+"F7.opExtrude","SWEPT_FACE",FACE,{"disambiguationData":[OSD([sQuery(id+"F6.wireOp",EDGE,"E18.4.16.0")])]})]});
            var Q38;
            Q38=makeQuery(id+"F7.boolean.opBoolean","INTERSECT",EDGE,{"derivedFrom":[makeQuery(id+"F1.opRevolve","SWEPT_FACE",FACE,{"disambiguationData":[OSD([sQuery(id+"F0.wireOp",EDGE,"E1.top")])]}),makeQuery(id+"F7.opExtrude","SWEPT_FACE",FACE,{"disambiguationData":[OSD([sQuery(id+"F6.wireOp",EDGE,"E18.4.15.0")])]})]});
            var Q39;
            Q39=makeQuery(id+"F7.boolean.opBoolean","INTERSECT",EDGE,{"derivedFrom":[makeQuery(id+"F1.opRevolve","SWEPT_FACE",FACE,{"disambiguationData":[OSD([sQuery(id+"F0.wireOp",EDGE,"E1.top")])]}),makeQuery(id+"F7.opExtrude","SWEPT_FACE",FACE,{"disambiguationData":[OSD([sQuery(id+"F6.wireOp",EDGE,"E17.1.14.0")])]})]});
            var Q40;
            Q40=makeQuery(id+"F7.boolean.opBoolean","INTERSECT",EDGE,{"derivedFrom":[makeQuery(id+"F1.opRevolve","SWEPT_FACE",FACE,{"disambiguationData":[OSD([sQuery(id+"F0.wireOp",EDGE,"E1.top")])]}),makeQuery(id+"F7.opExtrude","SWEPT_FACE",FACE,{"disambiguationData":[OSD([sQuery(id+"F6.wireOp",EDGE,"E17.4.14.0")])]})]});
            var Q41;
            Q41=makeQuery(id+"F7.boolean.opBoolean","INTERSECT",EDGE,{"derivedFrom":[makeQuery(id+"F1.opRevolve","SWEPT_FACE",FACE,{"disambiguationData":[OSD([sQuery(id+"F0.wireOp",EDGE,"E1.top")])]}),makeQuery(id+"F7.opExtrude","SWEPT_FACE",FACE,{"disambiguationData":[OSD([sQuery(id+"F6.wireOp",EDGE,"E15.1.6.0")])]})]});
            var Q42;
            Q42=makeQuery(id+"F7.boolean.opBoolean","INTERSECT",EDGE,{"derivedFrom":[makeQuery(id+"F1.opRevolve","SWEPT_FACE",FACE,{"disambiguationData":[OSD([sQuery(id+"F0.wireOp",EDGE,"E1.top")])]}),makeQuery(id+"F7.opExtrude","SWEPT_FACE",FACE,{"disambiguationData":[OSD([sQuery(id+"F6.wireOp",EDGE,"E17.1.13.0")])]})]});
            var Q43;
            Q43=makeQuery(id+"F7.boolean.opBoolean","INTERSECT",EDGE,{"derivedFrom":[makeQuery(id+"F1.opRevolve","SWEPT_FACE",FACE,{"disambiguationData":[OSD([sQuery(id+"F0.wireOp",EDGE,"E1.top")])]}),makeQuery(id+"F7.opExtrude","SWEPT_FACE",FACE,{"disambiguationData":[OSD([sQuery(id+"F6.wireOp",EDGE,"E18.1.15.0")])]})]});
            fillet(context, id + "F8", {"entities" : qUnion([Q0, Q1, Q2, Q3, Q4, Q5, Q6, Q7, Q8, Q9, Q10, Q11, Q12, Q13, Q14, Q15, Q16, Q17, Q18, Q19, Q20, Q21, Q22, Q23, Q24, Q25, Q26, Q27, Q28, Q29, Q30, Q31, Q32, Q33, Q34, Q35, Q36, Q37, Q38, Q39, Q40, Q41, Q42, Q43]), "radius" : 2.54 * mm, "tangentPropagation" : true, "allowEdgeOverflow" : false});
        }
    });
